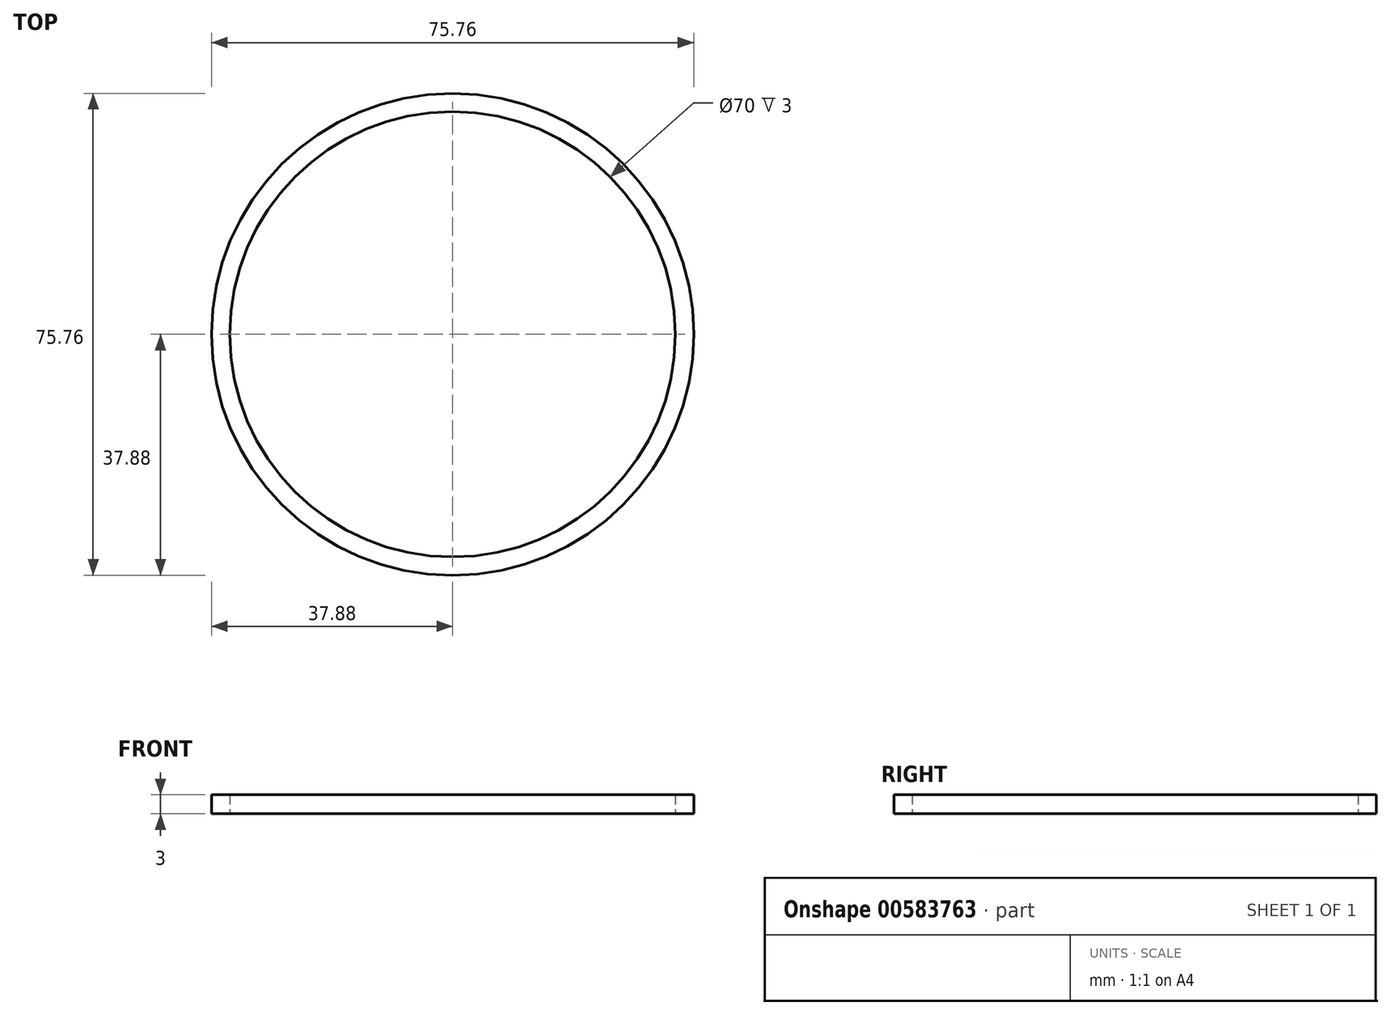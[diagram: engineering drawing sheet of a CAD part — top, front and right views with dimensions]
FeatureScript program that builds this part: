
annotation { "Feature Type Name" : "Feature", "Feature Type Description" : "" }
export const myFeature = defineFeature(function(context is Context, id is Id, definition is map)
    precondition{}
    {
        {
            var Q0;
            Q0=qCreatedBy(makeId("Top.planeOp"),FACE);
            var sketch = newSketch(context, id + "F0", { "sketchPlane" : qUnion([Q0])});
            skCircle(sketch, "E0", {"center": v(0, 0) * mm, "radius": 35 * mm});
            skCircle(sketch, "E1.0", {"center": v(0, 0) * mm, "radius": 37.88 * mm});
            skSolve(sketch);
        }
        {
            var Q0;
            Q0=makeQuery(id+"F0.imprint","IMPRINT",FACE,{"disambiguationData":[TD([[makeQuery(id+"F0.imprint","IMPRINT",EDGE,{"derivedFrom":sQuery(id+"F0.wireOp",EDGE,"E0")}),-1.0]])]});
            extrude(context, id + "F1", {"entities" : qUnion([Q0]), "depth" : 3 * mm, "offsetDistance" : 25 * mm});
        }
    });
